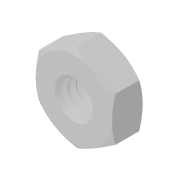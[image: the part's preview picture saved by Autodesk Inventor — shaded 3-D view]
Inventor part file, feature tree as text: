
AUTODESK INVENTOR PART (.ipt)
format: ipt  version: 2018 (Build 220112000, 112)  size: 292,352 bytes
history: native  units: in
note: dims shown in document units (in); Inventor stores cm internally (conversion verified against a paired STEP export)
features: mirror x1
ambient origin geometry x8: Origin, YZ Plane, XZ Plane, XY Plane, X Axis, Y Axis, Z Axis, Center Point
bodies: Solid1 (feature_tree)
feature tree (1):
  mirror  "Mirror2"
